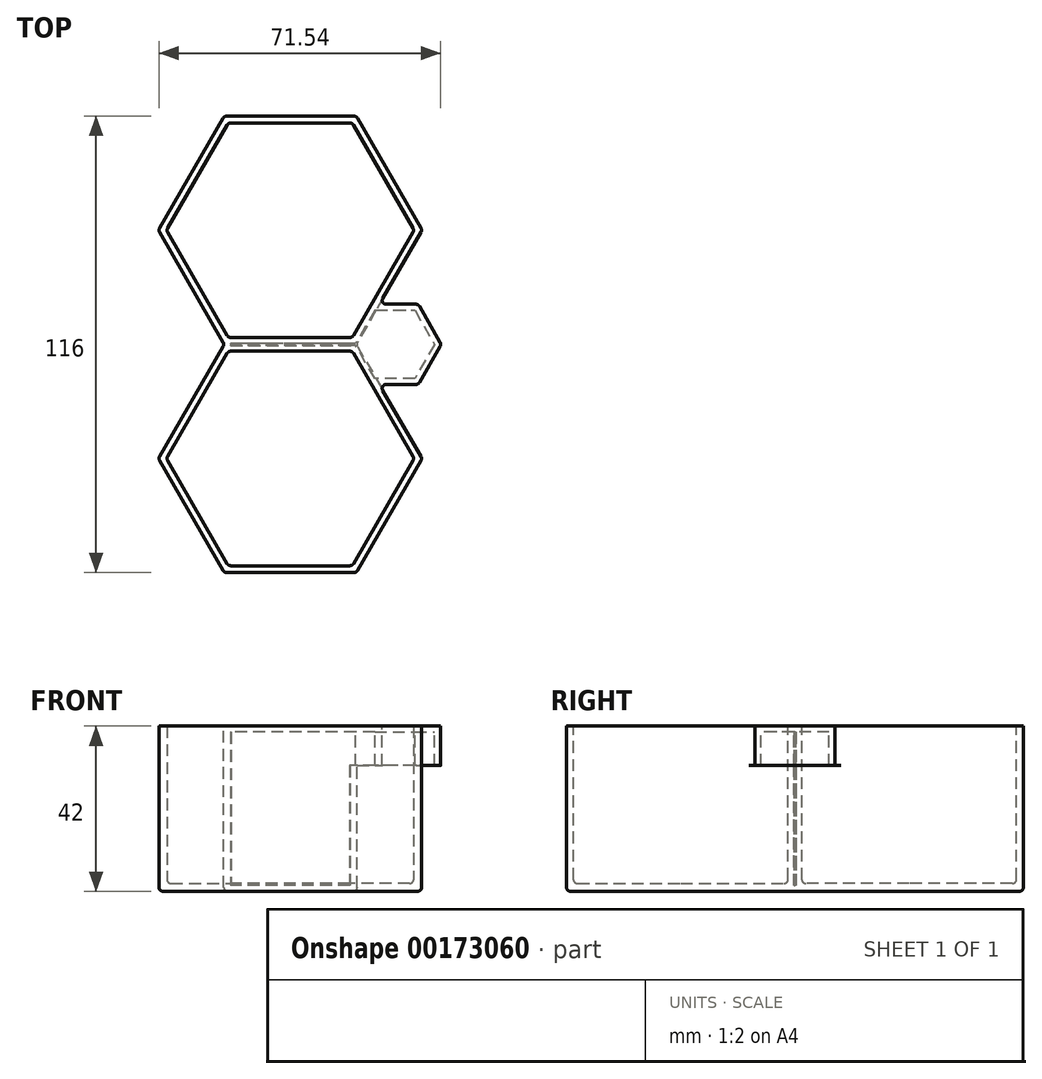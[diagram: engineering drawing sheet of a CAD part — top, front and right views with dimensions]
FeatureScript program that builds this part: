
annotation { "Feature Type Name" : "Feature", "Feature Type Description" : "" }
export const myFeature = defineFeature(function(context is Context, id is Id, definition is map)
    precondition{}
    {
        {
            var Q0;
            Q0=qCreatedBy(makeId("Top.planeOp"),FACE);
            var sketch = newSketch(context, id + "F0", { "sketchPlane" : qUnion([Q0])});
            skLineSegment(sketch, "E0.1", {"start": v(-16.74, 0) * mm, "end": v(-33.49, 29) * mm});
            skLineSegment(sketch, "E0.2", {"start": v(-33.49, 29) * mm, "end": v(-16.74, 58) * mm});
            skLineSegment(sketch, "E0.3", {"start": v(-16.74, 58) * mm, "end": v(16.74, 58) * mm});
            skLineSegment(sketch, "E0.4", {"start": v(16.74, 58) * mm, "end": v(33.49, 29) * mm});
            skLineSegment(sketch, "E0.5", {"start": v(33.49, 29) * mm, "end": v(16.74, 0) * mm});
            skLineSegment(sketch, "E1.1", {"start": v(16.74, 0) * mm, "end": v(33.49, -29) * mm});
            skLineSegment(sketch, "E1.2", {"start": v(33.49, -29) * mm, "end": v(16.74, -58) * mm});
            skLineSegment(sketch, "E1.3", {"start": v(16.74, -58) * mm, "end": v(-16.74, -58) * mm});
            skLineSegment(sketch, "E1.4", {"start": v(-16.74, -58) * mm, "end": v(-33.49, -29) * mm});
            skLineSegment(sketch, "E1.5", {"start": v(-33.49, -29) * mm, "end": v(-16.74, 0) * mm});
            skSolve(sketch);
        }
        {
            var Q0;
            Q0 = qSketchRegion(id + "F0", true);
            extrude(context, id + "F1", {"entities" : qUnion([Q0]), "depth" : 42 * mm});
        }
        {
            var Q0;
            Q0=makeQuery(id+"F1.opExtrude","CAP_FACE",FACE,{"disambiguationData":[OSD([sQuery(id+"F0.wireOp",EDGE,"E0.1"),sQuery(id+"F0.wireOp",EDGE,"E0.2"),sQuery(id+"F0.wireOp",EDGE,"E0.3"),sQuery(id+"F0.wireOp",EDGE,"E0.4"),sQuery(id+"F0.wireOp",EDGE,"E0.5"),sQuery(id+"F0.wireOp",EDGE,"E1.1"),sQuery(id+"F0.wireOp",EDGE,"E1.2"),sQuery(id+"F0.wireOp",EDGE,"E1.3"),sQuery(id+"F0.wireOp",EDGE,"E1.4"),sQuery(id+"F0.wireOp",EDGE,"E1.5")])],"isStart":false});
            var sketch = newSketch(context, id + "F2", { "sketchPlane" : qUnion([Q0])});
            skLineSegment(sketch, "E2", {"start": v(0, 0) * mm, "end": v(0, -29) * mm});
            skLineSegment(sketch, "E3", {"start": v(0, 0) * mm, "end": v(0, 29) * mm});
            skCircle(sketch, "E4.cCircle", {"center": v(0, 29) * mm, "radius": 27.25 * mm, "construction": true});
            skLineSegment(sketch, "E4.0", {"start": v(15.73, 1.75) * mm, "end": v(-15.73, 1.75) * mm});
            skLineSegment(sketch, "E4.1", {"start": v(-15.73, 1.75) * mm, "end": v(-31.47, 29) * mm});
            skLineSegment(sketch, "E4.2", {"start": v(-31.47, 29) * mm, "end": v(-15.73, 56.25) * mm});
            skLineSegment(sketch, "E4.3", {"start": v(-15.73, 56.25) * mm, "end": v(15.73, 56.25) * mm});
            skLineSegment(sketch, "E4.4", {"start": v(15.73, 56.25) * mm, "end": v(31.47, 29) * mm});
            skLineSegment(sketch, "E4.5", {"start": v(31.47, 29) * mm, "end": v(15.73, 1.75) * mm});
            skPoint(sketch, "E4.0.midPoint", {"position": v(0, 1.75) * mm});
            skCircle(sketch, "E5.cCircle", {"center": v(0, -29) * mm, "radius": 27.25 * mm, "construction": true});
            skLineSegment(sketch, "E5.0", {"start": v(-15.73, -1.75) * mm, "end": v(15.73, -1.75) * mm});
            skLineSegment(sketch, "E5.1", {"start": v(15.73, -1.75) * mm, "end": v(31.47, -29) * mm});
            skLineSegment(sketch, "E5.2", {"start": v(31.47, -29) * mm, "end": v(15.73, -56.25) * mm});
            skLineSegment(sketch, "E5.3", {"start": v(15.73, -56.25) * mm, "end": v(-15.73, -56.25) * mm});
            skLineSegment(sketch, "E5.4", {"start": v(-15.73, -56.25) * mm, "end": v(-31.47, -29) * mm});
            skLineSegment(sketch, "E5.5", {"start": v(-31.47, -29) * mm, "end": v(-15.73, -1.75) * mm});
            skPoint(sketch, "E5.0.midPoint", {"position": v(0, -1.75) * mm});
            skSolve(sketch);
        }
        {
            var Q0;
            {var subQ0=sQuery(id+"F2.wireOp",EDGE,"E5.1");Q0=makeQuery(id+"F2.imprint","IMPRINT",FACE,{"disambiguationData":[TD([[makeQuery(id+"F2.imprint","IMPRINT",EDGE,{"derivedFrom":subQ0}),-1.0]])]});}
            var Q1;
            {var subQ0=sQuery(id+"F2.wireOp",EDGE,"E4.1");Q1=makeQuery(id+"F2.imprint","IMPRINT",FACE,{"disambiguationData":[TD([[makeQuery(id+"F2.imprint","IMPRINT",EDGE,{"derivedFrom":subQ0}),-1.0]])]});}
            extrude(context, id + "F3", {"entities" : qUnion([Q0, Q1]), "operationType" : NewBodyOperationType.REMOVE, "oppositeDirection" : true, "depth" : 40 * mm});
        }
        {
            var Q0;
            Q0=makeQuery(id+"F1.opExtrude","CAP_FACE",FACE,{"disambiguationData":[OSD([sQuery(id+"F0.wireOp",EDGE,"E0.1"),sQuery(id+"F0.wireOp",EDGE,"E0.2"),sQuery(id+"F0.wireOp",EDGE,"E0.3"),sQuery(id+"F0.wireOp",EDGE,"E0.4"),sQuery(id+"F0.wireOp",EDGE,"E0.5"),sQuery(id+"F0.wireOp",EDGE,"E1.1"),sQuery(id+"F0.wireOp",EDGE,"E1.2"),sQuery(id+"F0.wireOp",EDGE,"E1.3"),sQuery(id+"F0.wireOp",EDGE,"E1.4"),sQuery(id+"F0.wireOp",EDGE,"E1.5")])],"isStart":false});
            var sketch = newSketch(context, id + "F4", { "sketchPlane" : qUnion([Q0])});
            skCircle(sketch, "E6.cCircle", {"center": v(26.6, 0) * mm, "radius": 10.19 * mm, "construction": true});
            skLineSegment(sketch, "E6.0", {"start": v(20.73, 10.19) * mm, "end": v(32.49, 10.19) * mm});
            skLineSegment(sketch, "E6.1", {"start": v(32.49, 10.19) * mm, "end": v(38.37, 0) * mm});
            skLineSegment(sketch, "E6.2", {"start": v(38.37, 0) * mm, "end": v(32.49, -10.19) * mm});
            skLineSegment(sketch, "E6.3", {"start": v(32.49, -10.19) * mm, "end": v(20.73, -10.19) * mm});
            skLineSegment(sketch, "E6.4", {"start": v(20.73, -10.19) * mm, "end": v(14.85, 0) * mm});
            skLineSegment(sketch, "E6.5", {"start": v(14.85, 0) * mm, "end": v(20.73, 10.19) * mm});
            skPoint(sketch, "E6.0.midPoint", {"position": v(26.6, 10.19) * mm});
            skSolve(sketch);
        }
        {
            var Q0;
            Q0 = qSketchRegion(id + "F4", true);
            extrude(context, id + "F5", {"entities" : qUnion([Q0]), "operationType" : NewBodyOperationType.ADD, "oppositeDirection" : true, "depth" : 10 * mm});
        }
        {
            var Q0;
            Q0=makeQuery(id+"F5.opExtrude","CAP_FACE",FACE,{"disambiguationData":[OSD([sQuery(id+"F4.wireOp",EDGE,"E6.0"),sQuery(id+"F4.wireOp",EDGE,"E6.1"),sQuery(id+"F4.wireOp",EDGE,"E6.2"),sQuery(id+"F4.wireOp",EDGE,"E6.3"),sQuery(id+"F4.wireOp",EDGE,"E6.4"),sQuery(id+"F4.wireOp",EDGE,"E6.5")])],"isStart":false});
            shell(context, id + "F6", {"entities" : qUnion([Q0]), "thickness" : 1.5 * mm});
        }
        {
            var Q0;
            Q0=makeQuery(id+"F1.opExtrude","SWEPT_EDGE",EDGE,{"disambiguationData":[OSD([sQuery(id+"F0.wireOp",EDGE,"E1.4"),sQuery(id+"F0.wireOp",EDGE,"E1.5")])]});
            var Q1;
            Q1=makeQuery(id+"F1.opExtrude","SWEPT_EDGE",EDGE,{"disambiguationData":[OSD([sQuery(id+"F0.wireOp",EDGE,"E0.1"),sQuery(id+"F0.wireOp",EDGE,"E1.5")])]});
            var Q2;
            Q2=makeQuery(id+"F1.opExtrude","SWEPT_EDGE",EDGE,{"disambiguationData":[OSD([sQuery(id+"F0.wireOp",EDGE,"E0.1"),sQuery(id+"F0.wireOp",EDGE,"E0.2")])]});
            var Q3;
            Q3=makeQuery(id+"F1.opExtrude","SWEPT_EDGE",EDGE,{"disambiguationData":[OSD([sQuery(id+"F0.wireOp",EDGE,"E0.2"),sQuery(id+"F0.wireOp",EDGE,"E0.3")])]});
            var Q4;
            Q4=makeQuery(id+"F1.opExtrude","SWEPT_EDGE",EDGE,{"disambiguationData":[OSD([sQuery(id+"F0.wireOp",EDGE,"E1.3"),sQuery(id+"F0.wireOp",EDGE,"E1.4")])]});
            var Q5;
            Q5=makeQuery(id+"F1.opExtrude","SWEPT_EDGE",EDGE,{"disambiguationData":[OSD([sQuery(id+"F0.wireOp",EDGE,"E1.2"),sQuery(id+"F0.wireOp",EDGE,"E1.3")])]});
            var Q6;
            Q6=makeQuery(id+"F1.opExtrude","SWEPT_EDGE",EDGE,{"disambiguationData":[OSD([sQuery(id+"F0.wireOp",EDGE,"E1.1"),sQuery(id+"F0.wireOp",EDGE,"E1.2")])]});
            var Q7;
            Q7=makeQuery(id+"F1.opExtrude","SWEPT_EDGE",EDGE,{"disambiguationData":[OSD([sQuery(id+"F0.wireOp",EDGE,"E0.5"),sQuery(id+"F0.wireOp",EDGE,"E1.1")])]});
            var Q8;
            Q8=makeQuery(id+"F1.opExtrude","SWEPT_EDGE",EDGE,{"disambiguationData":[OSD([sQuery(id+"F0.wireOp",EDGE,"E0.4"),sQuery(id+"F0.wireOp",EDGE,"E0.5")])]});
            var Q9;
            Q9=makeQuery(id+"F1.opExtrude","SWEPT_EDGE",EDGE,{"disambiguationData":[OSD([sQuery(id+"F0.wireOp",EDGE,"E0.3"),sQuery(id+"F0.wireOp",EDGE,"E0.4")])]});
            var Q10;
            Q10=makeQuery(id+"F3.boolean.opBoolean","COPY",EDGE,{"derivedFrom":makeQuery(id+"F3.opExtrude","SWEPT_EDGE",EDGE,{"disambiguationData":[OSD([sQuery(id+"F2.wireOp",EDGE,"E4.1"),sQuery(id+"F2.wireOp",EDGE,"E4.2")])]})});
            var Q11;
            Q11=makeQuery(id+"F3.boolean.opBoolean","COPY",EDGE,{"derivedFrom":makeQuery(id+"F3.opExtrude","SWEPT_EDGE",EDGE,{"disambiguationData":[OSD([sQuery(id+"F2.wireOp",EDGE,"E4.2"),sQuery(id+"F2.wireOp",EDGE,"E4.3")])]})});
            var Q12;
            Q12=makeQuery(id+"F3.boolean.opBoolean","COPY",EDGE,{"derivedFrom":makeQuery(id+"F3.opExtrude","SWEPT_EDGE",EDGE,{"disambiguationData":[OSD([sQuery(id+"F2.wireOp",EDGE,"E4.3"),sQuery(id+"F2.wireOp",EDGE,"E4.4")])]})});
            var Q13;
            Q13=makeQuery(id+"F3.boolean.opBoolean","COPY",EDGE,{"derivedFrom":makeQuery(id+"F3.opExtrude","SWEPT_EDGE",EDGE,{"disambiguationData":[OSD([sQuery(id+"F2.wireOp",EDGE,"E4.4"),sQuery(id+"F2.wireOp",EDGE,"E4.5")])]})});
            var Q14;
            Q14=makeQuery(id+"F3.boolean.opBoolean","COPY",EDGE,{"derivedFrom":makeQuery(id+"F3.opExtrude","SWEPT_EDGE",EDGE,{"disambiguationData":[OSD([sQuery(id+"F2.wireOp",EDGE,"E4.0"),sQuery(id+"F2.wireOp",EDGE,"E4.5")])]})});
            var Q15;
            Q15=makeQuery(id+"F3.boolean.opBoolean","COPY",EDGE,{"derivedFrom":makeQuery(id+"F3.opExtrude","SWEPT_EDGE",EDGE,{"disambiguationData":[OSD([sQuery(id+"F2.wireOp",EDGE,"E4.0"),sQuery(id+"F2.wireOp",EDGE,"E4.1")])]})});
            var Q16;
            Q16=makeQuery(id+"F3.boolean.opBoolean","COPY",EDGE,{"derivedFrom":makeQuery(id+"F3.opExtrude","SWEPT_EDGE",EDGE,{"disambiguationData":[OSD([sQuery(id+"F2.wireOp",EDGE,"E5.4"),sQuery(id+"F2.wireOp",EDGE,"E5.5")])]})});
            var Q17;
            Q17=makeQuery(id+"F3.boolean.opBoolean","COPY",EDGE,{"derivedFrom":makeQuery(id+"F3.opExtrude","SWEPT_EDGE",EDGE,{"disambiguationData":[OSD([sQuery(id+"F2.wireOp",EDGE,"E5.0"),sQuery(id+"F2.wireOp",EDGE,"E5.5")])]})});
            var Q18;
            Q18=makeQuery(id+"F3.boolean.opBoolean","COPY",EDGE,{"derivedFrom":makeQuery(id+"F3.opExtrude","SWEPT_EDGE",EDGE,{"disambiguationData":[OSD([sQuery(id+"F2.wireOp",EDGE,"E5.0"),sQuery(id+"F2.wireOp",EDGE,"E5.1")])]})});
            var Q19;
            Q19=makeQuery(id+"F3.boolean.opBoolean","COPY",EDGE,{"derivedFrom":makeQuery(id+"F3.opExtrude","SWEPT_EDGE",EDGE,{"disambiguationData":[OSD([sQuery(id+"F2.wireOp",EDGE,"E5.1"),sQuery(id+"F2.wireOp",EDGE,"E5.2")])]})});
            var Q20;
            Q20=makeQuery(id+"F3.boolean.opBoolean","COPY",EDGE,{"derivedFrom":makeQuery(id+"F3.opExtrude","SWEPT_EDGE",EDGE,{"disambiguationData":[OSD([sQuery(id+"F2.wireOp",EDGE,"E5.2"),sQuery(id+"F2.wireOp",EDGE,"E5.3")])]})});
            var Q21;
            Q21=makeQuery(id+"F3.boolean.opBoolean","COPY",EDGE,{"derivedFrom":makeQuery(id+"F3.opExtrude","SWEPT_EDGE",EDGE,{"disambiguationData":[OSD([sQuery(id+"F2.wireOp",EDGE,"E5.3"),sQuery(id+"F2.wireOp",EDGE,"E5.4")])]})});
            var Q22;
            Q22=makeQuery(id+"F3.boolean.opBoolean","COPY",FACE,{"derivedFrom":makeQuery(id+"F3.opExtrude","CAP_FACE",FACE,{"disambiguationData":[OSD([sQuery(id+"F2.wireOp",EDGE,"E4.0"),sQuery(id+"F2.wireOp",EDGE,"E4.1"),sQuery(id+"F2.wireOp",EDGE,"E4.2"),sQuery(id+"F2.wireOp",EDGE,"E4.3"),sQuery(id+"F2.wireOp",EDGE,"E4.4"),sQuery(id+"F2.wireOp",EDGE,"E4.5")])],"isStart":false})});
            var Q23;
            Q23=makeQuery(id+"F3.boolean.opBoolean","COPY",FACE,{"derivedFrom":makeQuery(id+"F3.opExtrude","CAP_FACE",FACE,{"disambiguationData":[OSD([sQuery(id+"F2.wireOp",EDGE,"E5.0"),sQuery(id+"F2.wireOp",EDGE,"E5.1"),sQuery(id+"F2.wireOp",EDGE,"E5.2"),sQuery(id+"F2.wireOp",EDGE,"E5.3"),sQuery(id+"F2.wireOp",EDGE,"E5.4"),sQuery(id+"F2.wireOp",EDGE,"E5.5")])],"isStart":false})});
            var Q24;
            Q24=makeQuery(id+"F1.opExtrude","CAP_FACE",FACE,{"disambiguationData":[OSD([sQuery(id+"F0.wireOp",EDGE,"E0.1"),sQuery(id+"F0.wireOp",EDGE,"E0.2"),sQuery(id+"F0.wireOp",EDGE,"E0.3"),sQuery(id+"F0.wireOp",EDGE,"E0.4"),sQuery(id+"F0.wireOp",EDGE,"E0.5"),sQuery(id+"F0.wireOp",EDGE,"E1.1"),sQuery(id+"F0.wireOp",EDGE,"E1.2"),sQuery(id+"F0.wireOp",EDGE,"E1.3"),sQuery(id+"F0.wireOp",EDGE,"E1.4"),sQuery(id+"F0.wireOp",EDGE,"E1.5")])],"isStart":true});
            var Q25;
            Q25=makeQuery(id+"F5.boolean.opBoolean","INTERSECT",EDGE,{"derivedFrom":[makeQuery(id+"F1.opExtrude","SWEPT_FACE",FACE,{"disambiguationData":[OSD([sQuery(id+"F0.wireOp",EDGE,"E0.5")])]}),makeQuery(id+"F5.opExtrude","SWEPT_FACE",FACE,{"disambiguationData":[OSD([sQuery(id+"F4.wireOp",EDGE,"E6.0")])]})]});
            var Q26;
            Q26=makeQuery(id+"F5.opExtrude","SWEPT_EDGE",EDGE,{"disambiguationData":[OSD([sQuery(id+"F4.wireOp",EDGE,"E6.0"),sQuery(id+"F4.wireOp",EDGE,"E6.1")])]});
            var Q27;
            Q27=makeQuery(id+"F5.opExtrude","SWEPT_EDGE",EDGE,{"disambiguationData":[OSD([sQuery(id+"F4.wireOp",EDGE,"E6.1"),sQuery(id+"F4.wireOp",EDGE,"E6.2")])]});
            var Q28;
            Q28=makeQuery(id+"F5.opExtrude","SWEPT_EDGE",EDGE,{"disambiguationData":[OSD([sQuery(id+"F4.wireOp",EDGE,"E6.2"),sQuery(id+"F4.wireOp",EDGE,"E6.3")])]});
            var Q29;
            Q29=makeQuery(id+"F5.boolean.opBoolean","INTERSECT",EDGE,{"derivedFrom":[makeQuery(id+"F1.opExtrude","SWEPT_FACE",FACE,{"disambiguationData":[OSD([sQuery(id+"F0.wireOp",EDGE,"E1.1")])]}),makeQuery(id+"F5.opExtrude","SWEPT_FACE",FACE,{"disambiguationData":[OSD([sQuery(id+"F4.wireOp",EDGE,"E6.3")])]})]});
            fillet(context, id + "F7", {"entities" : qUnion([Q0, Q1, Q2, Q3, Q4, Q5, Q6, Q7, Q8, Q9, Q10, Q11, Q12, Q13, Q14, Q15, Q16, Q17, Q18, Q19, Q20, Q21, Q22, Q23, Q24, Q25, Q26, Q27, Q28, Q29]), "radius" : 1 * mm, "tangentPropagation" : true, "allowEdgeOverflow" : false});
        }
        {
            var Q0;
            Q0=makeQuery(id+"F3.boolean.opBoolean","COPY",FACE,{"derivedFrom":makeQuery(id+"F3.opExtrude","CAP_FACE",FACE,{"disambiguationData":[OSD([sQuery(id+"F2.wireOp",EDGE,"E4.0"),sQuery(id+"F2.wireOp",EDGE,"E4.1"),sQuery(id+"F2.wireOp",EDGE,"E4.2"),sQuery(id+"F2.wireOp",EDGE,"E4.3"),sQuery(id+"F2.wireOp",EDGE,"E4.4"),sQuery(id+"F2.wireOp",EDGE,"E4.5")])],"isStart":false})});
            var sketch = newSketch(context, id + "F8", { "sketchPlane" : qUnion([Q0])});
            skSolve(sketch);
        }
    });
